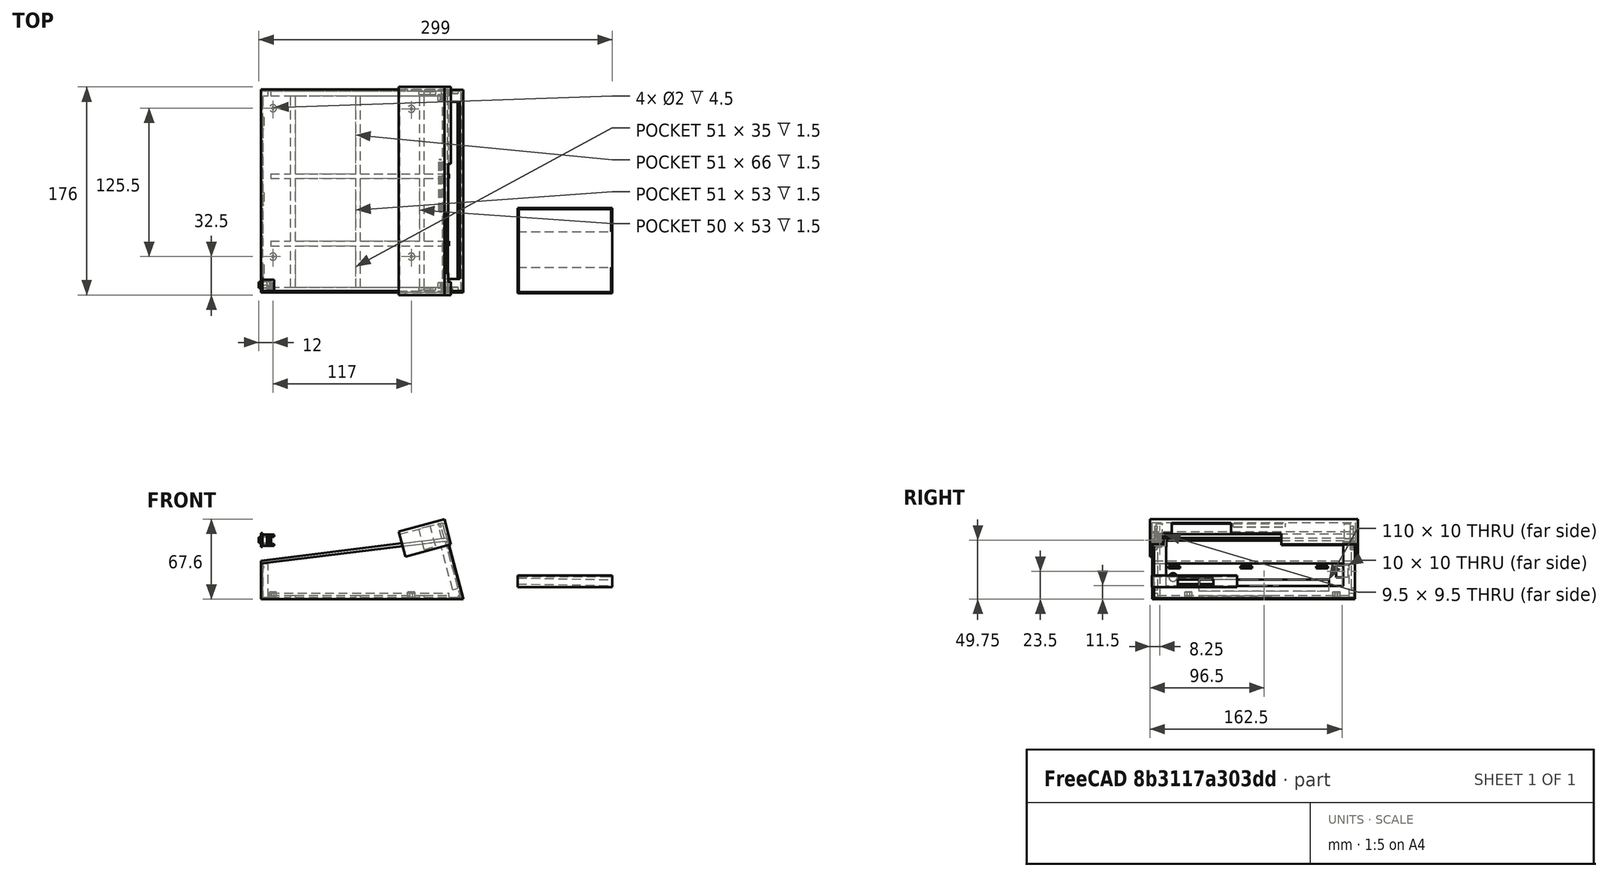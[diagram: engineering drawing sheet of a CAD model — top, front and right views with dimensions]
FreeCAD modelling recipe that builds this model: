
FCSTD DOCUMENT  (FreeCAD 0.20R29603 (Git))
Label: case4
License: All rights reserved
LicenseURL: http://en.wikipedia.org/wiki/All_rights_reserved
objects: Part::Box×40, Part::Cut×16, Part::MultiFuse×9, App::DocumentObjectGroup×9, Part::Cylinder×7, Part::FeaturePython×4
note: 76 computed .brp shape members not serialized (recipe doc carries the construction recipe); baked Part::Feature solids carry a one-line shape summary decoded from their .brp

FEATURE [Part::Box] Box  label="base"
  AttacherType = Attacher::AttachEngine3D
  Height = 1.5
  Length = 170
  Placement = pos=(0,0,-10) rot=(1,0,0;0rad)
  Width = 170
FEATURE [Part::Box] Box001  label="Face"
  AttacherType = Attacher::AttachEngine3D
  Height = 50
  Length = 2
  Placement = pos=(169,0,-10) rot=(0,-1,0;0.261799rad)
  Width = 170
FEATURE [Part::Box] Box002  label="Cube002"
  AttacherType = Attacher::AttachEngine3D
  Height = 28.5
  Length = 1.5
  Placement = pos=(0,0,-10) rot=(0,0,1;0rad)
  Width = 170
FEATURE [Part::FeaturePython] Tube002  # WARN: FeaturePython — macro-defined, semantics opaque (R4)
  AttacherType = Attacher::AttachEngine3D
  Height = 5
  InnerRadius = 1
  OuterRadius = 3
  Placement = pos=(10,10,-9) rot=(0,0,1;0rad)
FEATURE [Part::FeaturePython] Tube003  # WARN: FeaturePython — macro-defined, semantics opaque (R4)
  AttacherType = Attacher::AttachEngine3D
  Height = 5
  InnerRadius = 1
  OuterRadius = 3
  Placement = pos=(10,135.5,-9) rot=(0,0,1;0rad)
FEATURE [Part::FeaturePython] Tube004  # WARN: FeaturePython — macro-defined, semantics opaque (R4)
  AttacherType = Attacher::AttachEngine3D
  Height = 5
  InnerRadius = 1
  OuterRadius = 3
  Placement = pos=(127,135,-9) rot=(0,0,1;0rad)
FEATURE [Part::FeaturePython] Tube005  # WARN: FeaturePython — macro-defined, semantics opaque (R4)
  AttacherType = Attacher::AttachEngine3D
  Height = 5
  InnerRadius = 1
  OuterRadius = 3
  Placement = pos=(127,10,-9) rot=(0,0,1;0rad)
FEATURE [Part::Box] Box004  label="Cube003"
  AttacherType = Attacher::AttachEngine3D
  Height = 10
  Length = 10
  Placement = pos=(-3,38,-5) rot=(0,0,1;0rad)
  Width = 110
FEATURE [Part::MultiFuse] Fusion003
  Placement = pos=(0,20,0) rot=(0,0,1;0rad)
  Shapes = -> [Tube002,Tube003,Tube004,Tube005]
FEATURE [Part::Cylinder] Cylinder004  label="pwrjack"
  Angle = 360
  AttacherType = Attacher::AttachEngine3D
  FirstAngle = 0
  Height = 10
  Placement = pos=(-3,16,7) rot=(0,1,0;1.5708rad)
  Radius = 3.5
  SecondAngle = 0
FEATURE [Part::Cut] Cut003
  Base = -> Box002
  Tool = -> Cylinder004
FEATURE [Part::Cut] Cut
  Base = -> Cut003
  Tool = -> Box004
FEATURE [Part::Box] Box020  label="Face001"
  AttacherType = Attacher::AttachEngine3D
  Height = 40
  Length = 24
  Placement = pos=(164,10,0) rot=(0,-1,0;0.261799rad)
  Width = 150
FEATURE [Part::Cut] Cut005
  Base = -> Box001
  Tool = -> Box020
FEATURE [Part::Box] Box021  label="reset"
  AttacherType = Attacher::AttachEngine3D
  Height = 10
  Length = 10
  Placement = pos=(-2,154,7) rot=(0,0,1;0rad)
  Width = 10
FEATURE [Part::Cut] Cut006
  Base = -> Cut
  Placement = pos=(0,0,1.5) rot=(0,0,1;0rad)
  Tool = -> Box021
FEATURE [Part::Box] Box005  label="top"
  AttacherType = Attacher::AttachEngine3D
  Height = 2.5
  Length = 159
  Placement = pos=(0,0,20) rot=(0,-1,0;0.122173rad)
  Width = 170.5
FEATURE [App::DocumentObjectGroup] Group001  label="CaseTop"
  Group = -> [Box005]
FEATURE [Part::Box] Box022  label="Cube"
  AttacherType = Attacher::AttachEngine3D
  Height = 49
  Length = 171
  Placement = pos=(0,0,-10) rot=(0,0,1;0rad)
  Width = 1.5
FEATURE [Part::Box] Box023  label="Face002"
  AttacherType = Attacher::AttachEngine3D
  Height = 53
  Length = 25
  Placement = pos=(171,-14,-10) rot=(0,-1,0;0.261799rad)
  Width = 170
FEATURE [Part::Cut] Cut007
  Base = -> Box022
  Tool = -> Box023
FEATURE [Part::Box] Box024  label="top001"
  AttacherType = Attacher::AttachEngine3D
  Height = 20.5
  Length = 159
  Placement = pos=(0,0,20) rot=(0,-1,0;0.122173rad)
  Width = 170.5
FEATURE [Part::Cut] Cut008  label="sidewall"
  Base = -> Cut007
  Placement = pos=(0,-1.5,0) rot=(0,0,1;0rad)
  Tool = -> Box024
FEATURE [Part::Cylinder] Cylinder
  Angle = 360
  AttacherType = Attacher::AttachEngine3D
  FirstAngle = 0
  Height = 10
  Placement = pos=(1.5,22,17) rot=(1,0,0;1.5708rad)
  Radius = 1
  SecondAngle = 0
FEATURE [Part::Cylinder] Cylinder005
  Angle = 360
  AttacherType = Attacher::AttachEngine3D
  FirstAngle = 0
  Height = 10
  Placement = pos=(1.5,83,17) rot=(1,0,0;1.5708rad)
  Radius = 1
  SecondAngle = 0
FEATURE [Part::Cylinder] Cylinder006
  Angle = 360
  AttacherType = Attacher::AttachEngine3D
  FirstAngle = 0
  Height = 10
  Placement = pos=(1.5,147,17) rot=(1,0,0;1.5708rad)
  Radius = 1
  SecondAngle = 0
FEATURE [App::DocumentObjectGroup] Group003  label="Side1"
  Group = -> [Cut008]
FEATURE [Part::Box] Box025  label="Cube004"
  AttacherType = Attacher::AttachEngine3D
  Height = 28.5
  Length = 5
  Placement = pos=(1,0,-8.5) rot=(0,0,1;0rad)
  Width = 5
FEATURE [Part::Box] Box026  label="Cube005"
  AttacherType = Attacher::AttachEngine3D
  Height = 28.5
  Length = 5
  Placement = pos=(1,165,-8.5) rot=(0,0,1;0rad)
  Width = 5
FEATURE [Part::MultiFuse] Fusion
  Shapes = -> [Box025,Cut006,Cylinder,Cylinder005,Cylinder006,Box026]
FEATURE [App::DocumentObjectGroup] Group002  label="Back"
  Group = -> [Fusion]
FEATURE [Part::Box] Box027  label="Cube006"
  AttacherType = Attacher::AttachEngine3D
  Height = 4
  Length = 151
  Placement = pos=(8,0,-9) rot=(0,0,1;0rad)
  Width = 4
FEATURE [Part::Box] Box028  label="Cube007"
  AttacherType = Attacher::AttachEngine3D
  Height = 4
  Length = 151
  Placement = pos=(8,166,-9) rot=(0,0,1;0rad)
  Width = 4
FEATURE [Part::Box] Box029  label="Face003"
  AttacherType = Attacher::AttachEngine3D
  Height = 55
  Length = 2
  Placement = pos=(169.2,0,-11) rot=(0,-1,0;0.261799rad)
  Width = 170
FEATURE [Part::MultiFuse] Fusion005
  Shapes = -> [Box027,Box028,Fusion003]
FEATURE [Part::Cut] Cut009
  Base = -> Fusion005
  Tool = -> Box029
FEATURE [Part::Cylinder] Cylinder007
  Angle = 360
  AttacherType = Attacher::AttachEngine3D
  FirstAngle = 0
  Height = 47
  Placement = pos=(167.4,94,-8.1) rot=(1,0,0;1.5708rad)
  Radius = 1
  SecondAngle = 0
FEATURE [Part::Box] Box030  label="Cube008"
  AttacherType = Attacher::AttachEngine3D
  Height = 37
  Length = 5
  Placement = pos=(162,0,-2) rot=(0,-1,0;0.261799rad)
  Width = 3
FEATURE [Part::Box] Box031  label="Cube009"
  AttacherType = Attacher::AttachEngine3D
  Height = 37
  Length = 5
  Placement = pos=(162,167,-2) rot=(0,-1,0;0.261799rad)
  Width = 3
FEATURE [Part::MultiFuse] Fusion007
  Shapes = -> [Cut005,Box030,Box031]
FEATURE [App::DocumentObjectGroup] Group004  label="Front"
  Group = -> [Fusion007]
FEATURE [Part::Box] Box032  label="Cube010"
  AttacherType = Attacher::AttachEngine3D
  Height = 10
  Length = 80
  Placement = pos=(217,-2,0) rot=(0,0,1;0rad)
  Width = 72
FEATURE [Part::Box] Box033  label="Cube011"
  AttacherType = Attacher::AttachEngine3D
  Height = 5
  Length = 100
  Placement = pos=(206,20,3) rot=(0,1,0;0.017453rad)
  Width = 30
FEATURE [Part::Box] Box034  label="Cube012"
  AttacherType = Attacher::AttachEngine3D
  Height = 10
  Length = 78
  Placement = pos=(218,-1,9) rot=(0,0,1;0rad)
  Width = 70
FEATURE [Part::Cut] Cut010
  Base = -> Box032
  Tool = -> Box033
FEATURE [Part::Cut] Cut011
  Base = -> Cut010
  Tool = -> Box034
FEATURE [Part::Box] Box035  label="Cube013"
  AttacherType = Attacher::AttachEngine3D
  Height = 5
  Length = 91
  Placement = pos=(293,20,9) rot=(0,0,1;0rad)
  Width = 30
FEATURE [Part::Cut] Cut012
  Base = -> Cut011
  Tool = -> Box035
FEATURE [App::DocumentObjectGroup] Group005  label="keypad"
  Group = -> [Cut012]
FEATURE [Part::Box] Box036  label="Cube014"
  AttacherType = Attacher::AttachEngine3D
  Height = 2
  Length = 151
  Placement = pos=(8,96,-9) rot=(0,0,1;0rad)
  Width = 4
FEATURE [Part::Box] Box037  label="Cube015"
  AttacherType = Attacher::AttachEngine3D
  Height = 2
  Length = 151
  Placement = pos=(8,39,-9) rot=(0,0,1;0rad)
  Width = 4
FEATURE [Part::Box] Box038  label="Cube016"
  AttacherType = Attacher::AttachEngine3D
  Height = 2
  Length = 170
  Placement = pos=(29,0,-9) rot=(0,0,1;1.5708rad)
  Width = 4
FEATURE [Part::Box] Box039  label="Cube017"
  AttacherType = Attacher::AttachEngine3D
  Height = 2
  Length = 170
  Placement = pos=(84,0,-9) rot=(0,0,1;1.5708rad)
  Width = 4
FEATURE [Part::Box] Box040  label="Cube018"
  AttacherType = Attacher::AttachEngine3D
  Height = 2
  Length = 170
  Placement = pos=(138,0,-9) rot=(0,0,1;1.5708rad)
  Width = 4
FEATURE [Part::MultiFuse] Fusion006
  Placement = pos=(0,-1,0) rot=(0,0,1;0rad)
  Refine = true
  Shapes = -> [Cut009,Cylinder007,Box036,Box037,Box038,Box039,Box040,Box]
FEATURE [App::DocumentObjectGroup] Group  label="CaseBase"
  Group = -> [Fusion006]
FEATURE [Part::Box] Box041  label="Cube019"
  AttacherType = Attacher::AttachEngine3D
  Height = 22
  Length = 40
  Placement = pos=(122,-3.5,26) rot=(0,-1,0;0.261799rad)
  Width = 176
FEATURE [Part::Box] Box042  label="Cube020"
  AttacherType = Attacher::AttachEngine3D
  Height = 23
  Length = 45
  Placement = pos=(122,7.5,12) rot=(0,-1,0;0.261799rad)
  Width = 100
FEATURE [Part::Cut] Cut013
  Base = -> Box041
  Tool = -> Box042
FEATURE [Part::Box] Box043  label="Cube021"
  AttacherType = Attacher::AttachEngine3D
  Height = 20
  Length = 40
  Placement = pos=(120,-1.5,25) rot=(0,-1,0;0.261799rad)
  Width = 172
FEATURE [Part::Cut] Cut014
  Base = -> Cut013
  Tool = -> Box043
FEATURE [Part::Box] Box044  label="Cube022"
  AttacherType = Attacher::AttachEngine3D
  Height = 3
  Length = 1.5
  Placement = pos=(151,67,51) rot=(0,-1,0;0.261799rad)
  Width = 44
FEATURE [Part::MultiFuse] Fusion008
  Shapes = -> [Cut014,Box044]
FEATURE [Part::Box] Box045  label="Cube023"
  AttacherType = Attacher::AttachEngine3D
  Height = 10
  Length = 10
  Placement = pos=(156,15,44) rot=(0,-1,0;0.261799rad)
  Width = 50
FEATURE [Part::Cut] Cut015
  Base = -> Fusion008
  Tool = -> Box045
FEATURE [Part::Box] Box046  label="Cube024"
  AttacherType = Attacher::AttachEngine3D
  Height = 15
  Length = 2
  Placement = pos=(153,2,41) rot=(0,-1,0;0.261799rad)
  Width = 5
FEATURE [Part::Box] Box047  label="Cube025"
  AttacherType = Attacher::AttachEngine3D
  Height = 20
  Length = 10
  Placement = pos=(138,0.5,32) rot=(0,-1,0;0.261799rad)
  Width = 2
FEATURE [Part::Box] Box048  label="Cube026"
  AttacherType = Attacher::AttachEngine3D
  Height = 15
  Length = 2
  Placement = pos=(153,161,41) rot=(0,-1,0;0.261799rad)
  Width = 5
FEATURE [Part::Box] Box049  label="Cube027"
  AttacherType = Attacher::AttachEngine3D
  Height = 20
  Length = 10
  Placement = pos=(138,166,32) rot=(0,-1,0;0.261799rad)
  Width = 2.5
FEATURE [Part::MultiFuse] Fusion009
  Shapes = -> [Cut015,Box046,Box047,Box048,Box049]
FEATURE [App::DocumentObjectGroup] Group006  label="LCDCap"
  Group = -> [Fusion009]
FEATURE [Part::Box] Box050  label="Cube028"
  AttacherType = Attacher::AttachEngine3D
  Height = 9.5
  Length = 11
  Placement = pos=(0,0,35) rot=(0,0,1;0rad)
  Width = 9.5
FEATURE [Part::Box] Box051  label="Cube029"
  AttacherType = Attacher::AttachEngine3D
  Height = 12
  Length = 1
  Placement = pos=(0,-1,34) rot=(0,0,1;0rad)
  Width = 12
FEATURE [Part::MultiFuse] Fusion010
  Shapes = -> [Box050,Box051]
FEATURE [Part::Cylinder] Cylinder008
  Angle = 360
  AttacherType = Attacher::AttachEngine3D
  FirstAngle = 0
  Height = 9
  Placement = pos=(-1,5,40) rot=(0,1,0;1.5708rad)
  Radius = 3
  SecondAngle = 0
FEATURE [Part::Cut] Cut016
  Base = -> Fusion010
  Tool = -> Cylinder008
FEATURE [Part::Box] Box052  label="Cube030"
  AttacherType = Attacher::AttachEngine3D
  Height = 7.5
  Length = 4.5
  Placement = pos=(5,-1,36) rot=(0,0,1;0rad)
  Width = 13
FEATURE [Part::Cut] Cut017
  Base = -> Cut016
  Tool = -> Box052
FEATURE [Part::Box] Box053  label="Cube031"
  AttacherType = Attacher::AttachEngine3D
  Height = 6
  Length = 4.5
  Placement = pos=(9,-1,36.75) rot=(0,0,1;0rad)
  Width = 13
FEATURE [Part::Cut] Cut018
  Base = -> Cut017
  Tool = -> Box053
FEATURE [App::DocumentObjectGroup] Group007  label="resetbutton-case"
  Group = -> [Cut018]
FEATURE [Part::Cylinder] Cylinder009
  Angle = 360
  AttacherType = Attacher::AttachEngine3D
  FirstAngle = 0
  Height = 10
  Placement = pos=(-2,5,40) rot=(0,1,0;1.5708rad)
  Radius = 2.5
  SecondAngle = 0
FEATURE [Part::Box] Box054  label="Cube032"
  AttacherType = Attacher::AttachEngine3D
  Height = 5.5
  Length = 1.5
  Placement = pos=(7,1,37) rot=(0,0,1;0rad)
  Width = 8
FEATURE [Part::MultiFuse] Fusion011
  Shapes = -> [Cylinder009,Box054]
FEATURE [App::DocumentObjectGroup] Group008  label="resetbutton"
  Group = -> [Fusion011]
